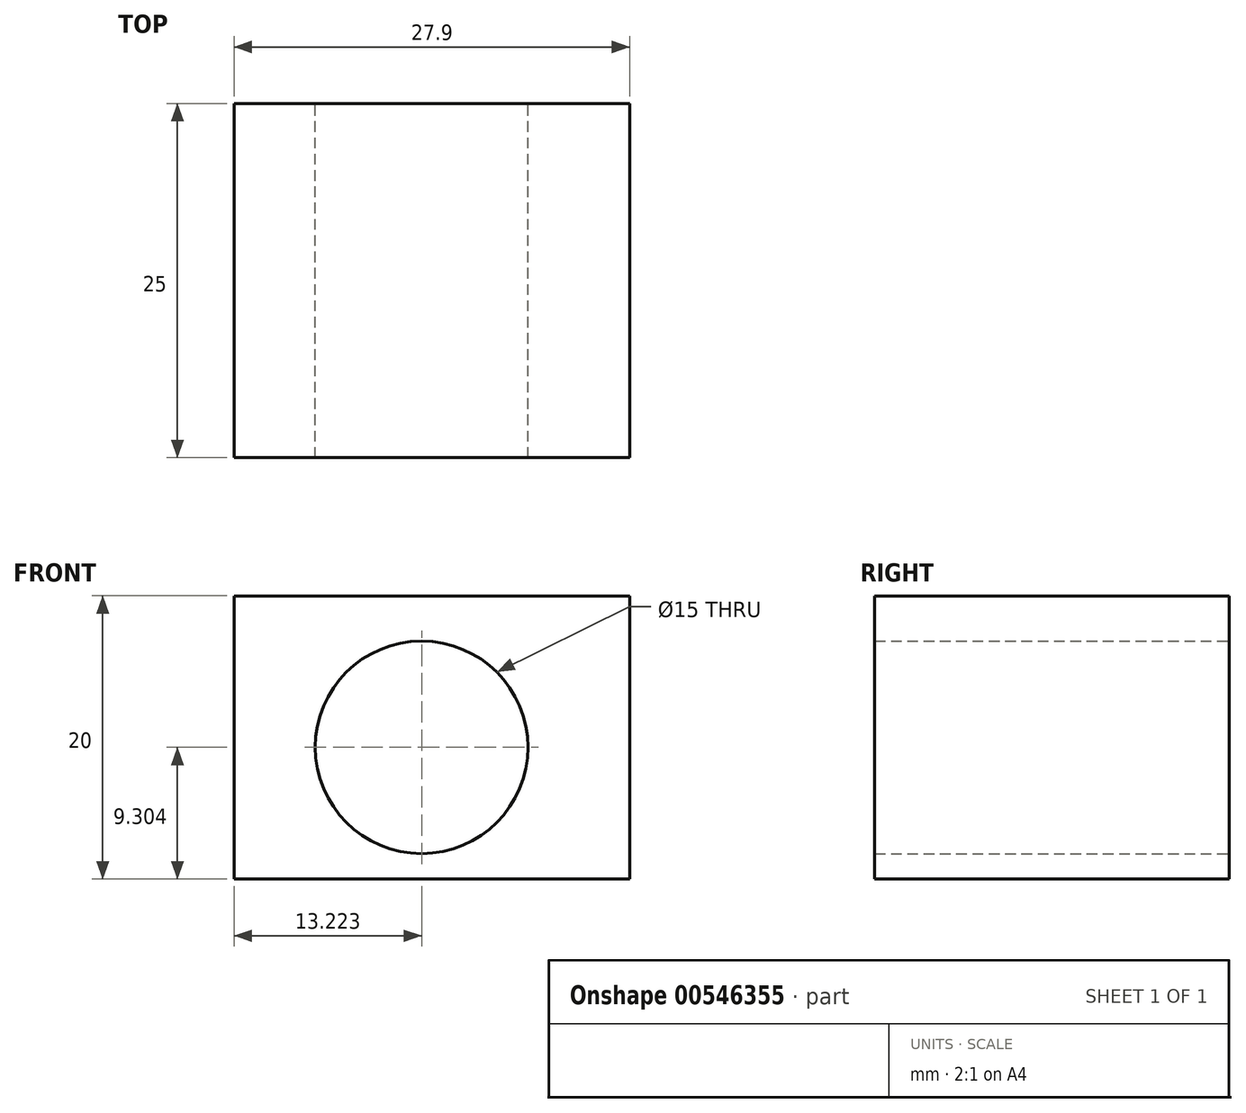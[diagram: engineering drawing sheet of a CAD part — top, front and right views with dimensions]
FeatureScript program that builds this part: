
annotation { "Feature Type Name" : "Feature", "Feature Type Description" : "" }
export const myFeature = defineFeature(function(context is Context, id is Id, definition is map)
    precondition{}
    {
        {
            var Q0;
            Q0=qCreatedBy(makeId("Front.planeOp"),FACE);
            var sketch = newSketch(context, id + "F0", { "sketchPlane" : qUnion([Q0])});
            skLineSegment(sketch, "E0.bottom", {"start": v(-11.6, 5.92) * mm, "end": v(16.31, 5.92) * mm});
            skLineSegment(sketch, "E0.top", {"start": v(-11.6, -14.08) * mm, "end": v(16.31, -14.08) * mm});
            skLineSegment(sketch, "E0.left", {"start": v(-11.6, 5.92) * mm, "end": v(-11.6, -14.08) * mm});
            skLineSegment(sketch, "E0.right", {"start": v(16.31, 5.92) * mm, "end": v(16.31, -14.08) * mm});
            skCircle(sketch, "E1", {"center": v(1.63, -4.78) * mm, "radius": 7.5 * mm});
            skSolve(sketch);
        }
        {
            var Q0;
            Q0=qSketchRegion(id+"F0",true);
            extrude(context, id + "F1", {"entities" : qUnion([Q0]), "depth" : 25 * mm, "offsetDistance" : 25 * mm});
        }
    });
